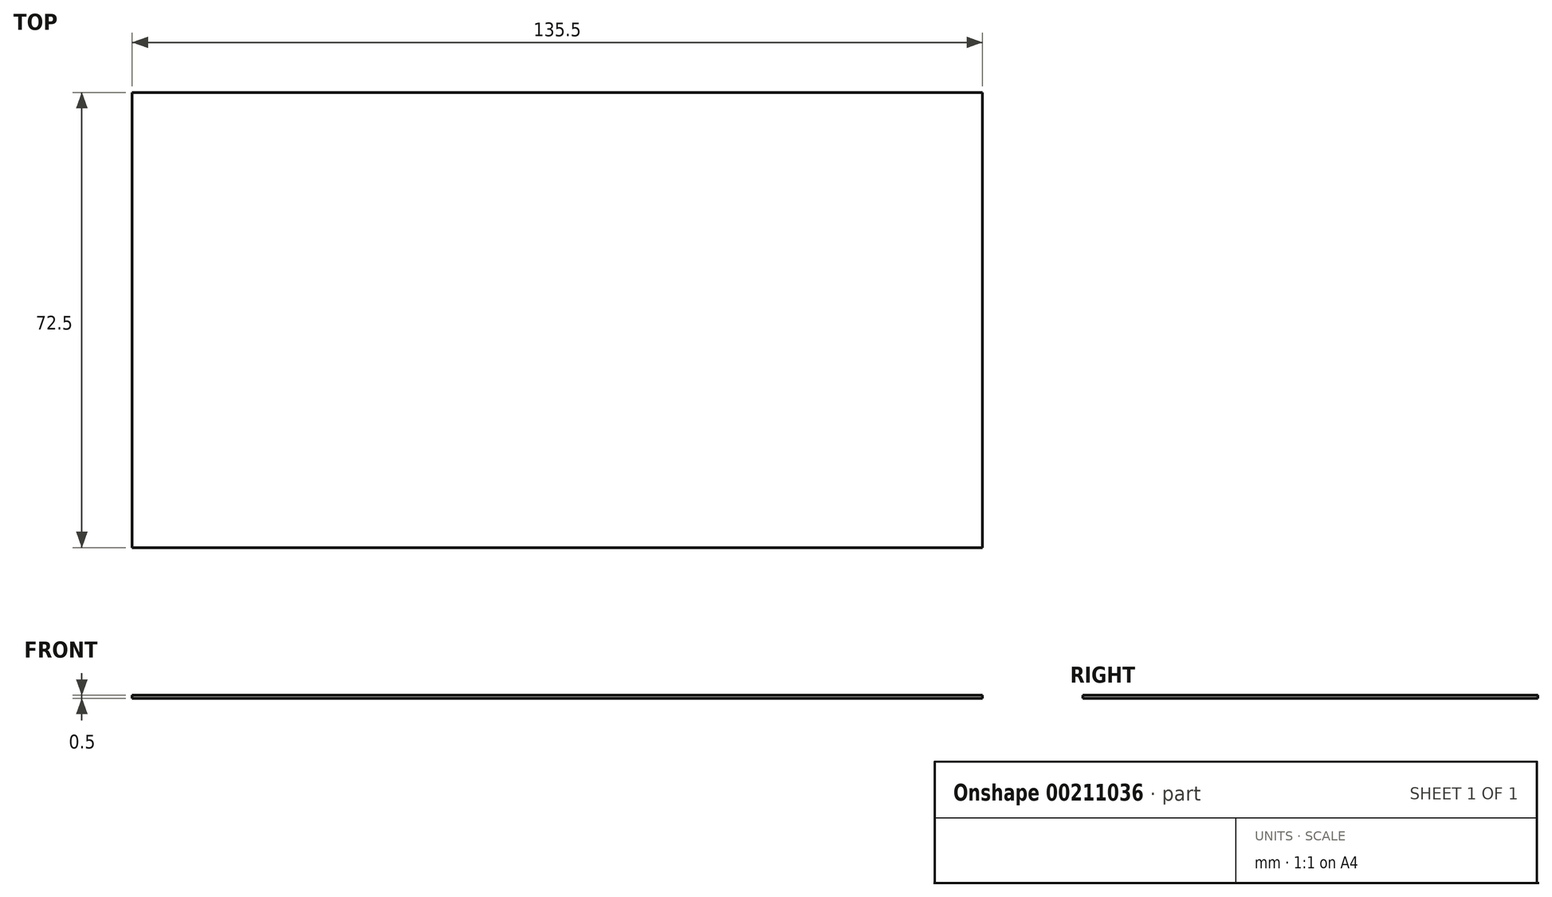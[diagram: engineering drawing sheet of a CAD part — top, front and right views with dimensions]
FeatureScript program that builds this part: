
annotation { "Feature Type Name" : "Feature", "Feature Type Description" : "" }
export const myFeature = defineFeature(function(context is Context, id is Id, definition is map)
    precondition{}
    {
        {
            var Q0;
            Q0=qCreatedBy(makeId("Top.planeOp"),FACE);
            var sketch = newSketch(context, id + "F0", { "sketchPlane" : qUnion([Q0])});
            skLineSegment(sketch, "E0.bottom", {"start": v(-67.75, -36.25) * mm, "end": v(67.75, -36.25) * mm});
            skLineSegment(sketch, "E0.top", {"start": v(-67.75, 36.25) * mm, "end": v(67.75, 36.25) * mm});
            skLineSegment(sketch, "E0.left", {"start": v(-67.75, -36.25) * mm, "end": v(-67.75, 36.25) * mm});
            skLineSegment(sketch, "E0.right", {"start": v(67.75, -36.25) * mm, "end": v(67.75, 36.25) * mm});
            skPoint(sketch, "E0.middle", {"position": v(0, 0) * mm});
            skSolve(sketch);
        }
        {
            var Q0;
            Q0=makeQuery(id+"F0.imprint","IMPRINT",FACE,{"disambiguationData":[TD([[makeQuery(id+"F0.imprint","IMPRINT",EDGE,{"derivedFrom":sQuery(id+"F0.wireOp",EDGE,"E0.bottom")}),1.0]])]});
            extrude(context, id + "F1", {"entities" : qUnion([Q0]), "depth" : 0.5 * mm});
        }
    });
